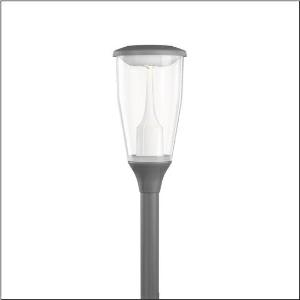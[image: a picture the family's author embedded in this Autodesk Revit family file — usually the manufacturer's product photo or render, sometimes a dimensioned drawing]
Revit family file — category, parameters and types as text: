
# Revit family: dl_11_iq___st1_2a_5xa5565af14hp00022_6a76
name_source: partatom
category: Lighting Fixtures
units: mm (PartAtom-declared; Revit-internal decimal feet)

## family parameters
Cut with Voids When Loaded = No
Host = Face
Light Source = No
Part Type = Normal
Room Calculation Point = No
Round Connector Dimension = Use Diameter
Shared = No

## types (1)
- --- (1 x LED, 4000 lm, 33.6 W, 2200K)
    Apparent Load = 34 VA
    CIE Flux Codes = 33 63 91 94 100
    Color Rendering = 70
    Color Temperature = 2200K
    Default Elevation = 1800 mm
    Description = DL 11 iQ, mast luminaire, Module 540 iQ-SR, primary light control with 3 zone facetted reflector, of plastic, silver coated, highly specular, structured, primary optical cover: cover, of PMMA, transparent, light distribution: ST1.2a, light emission: direct distribution, primary light characteristic: asymmetric, installation type: post-top, LED, High Power LED, light colour: 722, colour temperature: 2200K, control: Street-Remote, Auto-Match, Temp-Guard, Lumen-Switch, Night-Set, Smart-Wire, Light-Fading, Desk-Remote (wireless, voltage-free reading and setting of iQ features in the workshop via application-optimized NFC function/RFID function), optimised constant luminous flux control (CLO 2.0), mains connection: 220..240V, AC, 50/60Hz, connection cable pre-assembled, cable length: 5,5m, luminaire housing, upper part, of diecast aluminium, coated, Siteco® metallic grey (DB 702S), spigot size: 60mm (post-top), post-top mast mounting element, of diecast aluminium, coated, Siteco® metallic grey (DB 702S), Module 540 iQ-SR, traffic white (RAL 9016), equipment: Power, protection rating (complete): IP66, insulation class (complete): insulation class II (safety insulation), certification: CE, ENEC, ENEC+, VDE, packaging unit: 1 piece

Light Distribution: ST1.2a
    Height = 665 mm
    Lamp = 1 x LED
    Lamp Light Flux = 4000 lm
    Lamp Power = 33.6 W
    Lamp count = 1
    Length = 334 mm
    Luminous efficacy = 119 lm/W
    Manufacturer = Siteco
    ModVariant = No
    Model = 5XA5565AF14HP00022
    Number of Poles = 1
    OnlyDefault = Yes
    Power Factor = 1
    Product Name = DL 11 iQ | ST1.2a
    Product group = mast luminaire | pylon top
    ProductGroupID = 6100
    Protection Class = Protection class II
    Protection Degree = IP 66
    RLX_Detail_Level = 1
    RLX_Emergency_Light_Flux = 0 lm
    RLX_Emergency_Type = 0
    RLX_Emergency_Type_DB = No
    RlxData = <blob elided: 155065 chars, md5=f1591ca1>
    Socket = socket
    Standby Power = 0 W
    System Light Flux = 4000 lm
    System Power = 34 W
    Type Comments = factory setting: luminous flux: 100 % | dim-lin: 254 | 695 mA
    Type Image = l_1258354.jpg
    URL = http://relux.com
    VarID = @adj_020111
    Voltage = 0 V
    Weight = 0.00 kg
    Width = 0 mm  [stored 0 ft]

note: [stored X ft] marks values corroborated as IEEE doubles in the binary element streams (Revit-internal decimal feet)

## geometry (parser evidence)
native form markers: Blend x4, Sweep x9
no freeform markers — native parametric forms only
